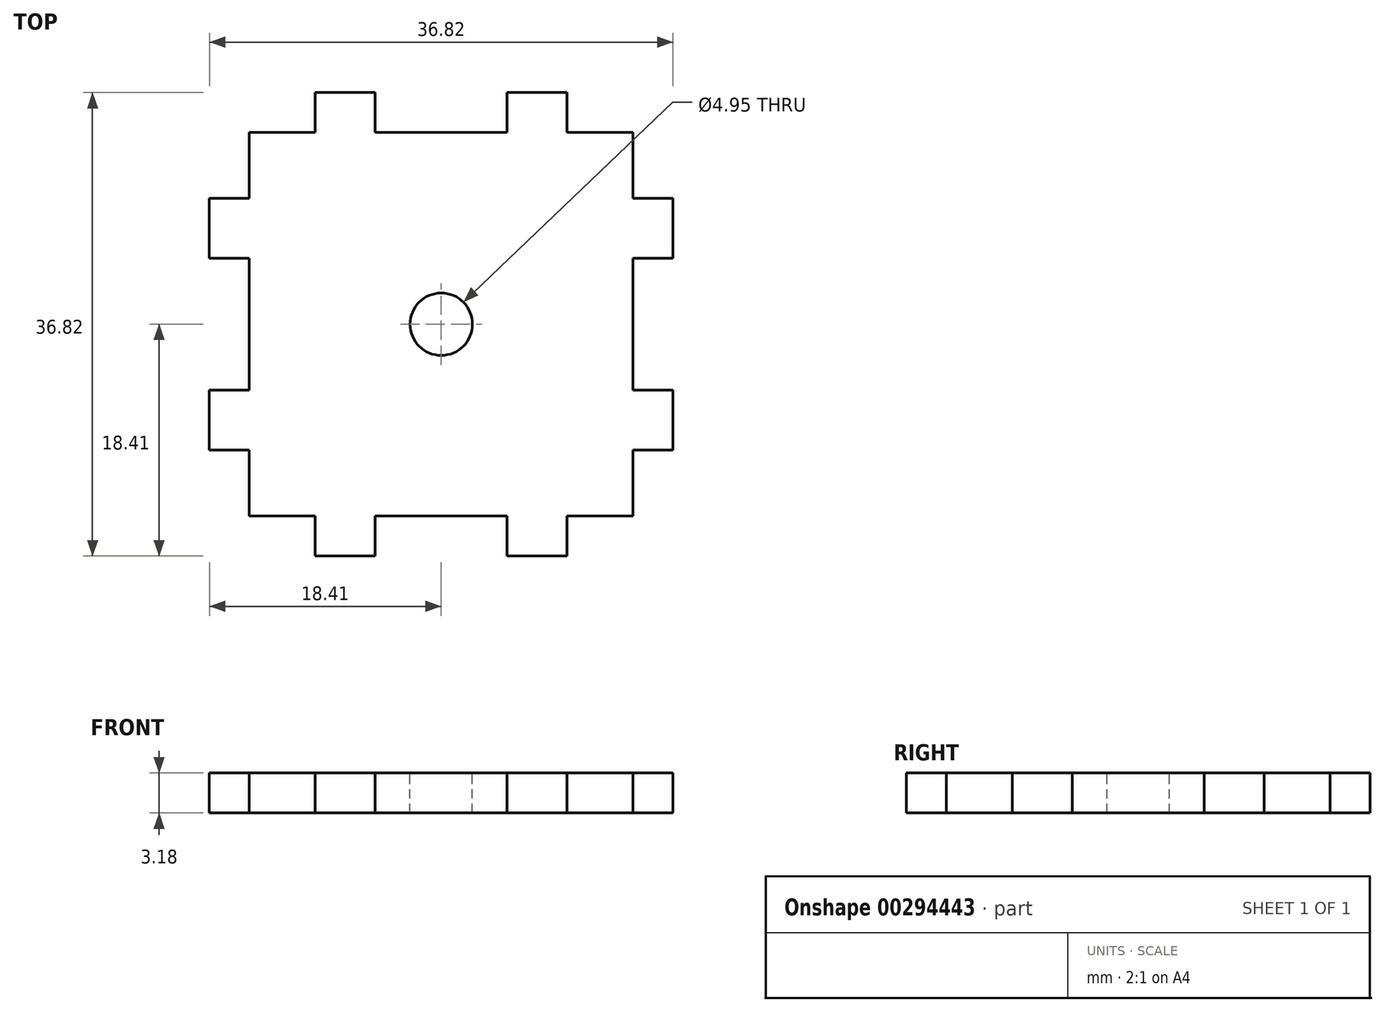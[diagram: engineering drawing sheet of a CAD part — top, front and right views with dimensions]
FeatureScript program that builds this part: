
annotation { "Feature Type Name" : "Feature", "Feature Type Description" : "" }
export const myFeature = defineFeature(function(context is Context, id is Id, definition is map)
    precondition{}
    {
        {
            var Q0;
            Q0=qCreatedBy(makeId("Top.planeOp"),FACE);
            var sketch = newSketch(context, id + "F0", { "sketchPlane" : qUnion([Q0])});
            skLineSegment(sketch, "E0.bottom", {"start": v(15.24, 15.24) * mm, "end": v(-15.24, 15.24) * mm});
            skLineSegment(sketch, "E0.top", {"start": v(15.24, -15.24) * mm, "end": v(-15.24, -15.24) * mm});
            skLineSegment(sketch, "E0.left", {"start": v(15.24, 15.24) * mm, "end": v(15.24, -15.24) * mm});
            skLineSegment(sketch, "E0.right", {"start": v(-15.24, 15.24) * mm, "end": v(-15.24, -15.24) * mm});
            skPoint(sketch, "E0.middle", {"position": v(0, 0) * mm});
            skLineSegment(sketch, "E1", {"start": v(0, 15.24) * mm, "end": v(0, -15.24) * mm});
            skLineSegment(sketch, "E2", {"start": v(-7.62, 15.24) * mm, "end": v(-7.62, -15.24) * mm});
            skLineSegment(sketch, "E3", {"start": v(7.62, 15.24) * mm, "end": v(7.62, -15.24) * mm});
            skLineSegment(sketch, "E4.bottom", {"start": v(-5.24, 18.41) * mm, "end": v(-10, 18.41) * mm});
            skLineSegment(sketch, "E4.top", {"start": v(-5.24, 12.06) * mm, "end": v(-10, 12.06) * mm});
            skLineSegment(sketch, "E4.left", {"start": v(-5.24, 18.41) * mm, "end": v(-5.24, 12.06) * mm});
            skLineSegment(sketch, "E4.right", {"start": v(-10, 18.41) * mm, "end": v(-10, 12.06) * mm});
            skPoint(sketch, "E4.middle", {"position": v(-7.62, 15.24) * mm});
            skLineSegment(sketch, "E5.bottom", {"start": v(10, 18.41) * mm, "end": v(5.24, 18.41) * mm});
            skLineSegment(sketch, "E5.top", {"start": v(10, 12.06) * mm, "end": v(5.24, 12.06) * mm});
            skLineSegment(sketch, "E5.left", {"start": v(10, 18.41) * mm, "end": v(10, 12.06) * mm});
            skLineSegment(sketch, "E5.right", {"start": v(5.24, 18.41) * mm, "end": v(5.24, 12.06) * mm});
            skPoint(sketch, "E5.middle", {"position": v(7.62, 15.24) * mm});
            skLineSegment(sketch, "E6", {"start": v(-15.24, 0) * mm, "end": v(15.24, 0) * mm});
            skLineSegment(sketch, "E7.MirrorCS", {"start": v(5.24, -18.41) * mm, "end": v(5.24, -12.06) * mm});
            skLineSegment(sketch, "E8.MirrorCS", {"start": v(10, -18.41) * mm, "end": v(5.24, -18.41) * mm});
            skLineSegment(sketch, "E9.MirrorCS", {"start": v(10, -18.41) * mm, "end": v(10, -12.06) * mm});
            skLineSegment(sketch, "E10.MirrorCS", {"start": v(7.62, -15.24) * mm, "end": v(7.62, 15.24) * mm});
            skLineSegment(sketch, "E11.MirrorCS", {"start": v(-5.24, -18.41) * mm, "end": v(-5.24, -12.06) * mm});
            skLineSegment(sketch, "E12.MirrorCS", {"start": v(-10, -18.41) * mm, "end": v(-10, -12.06) * mm});
            skLineSegment(sketch, "E13.MirrorCS", {"start": v(-5.24, -18.41) * mm, "end": v(-10, -18.41) * mm});
            skLineSegment(sketch, "E14.MirrorCS", {"start": v(-5.24, -12.06) * mm, "end": v(-10, -12.06) * mm});
            skLineSegment(sketch, "E15.MirrorCS", {"start": v(10, -12.06) * mm, "end": v(5.24, -12.06) * mm});
            skLineSegment(sketch, "E16", {"start": v(-15.24, 7.62) * mm, "end": v(15.24, 7.62) * mm});
            skLineSegment(sketch, "E17", {"start": v(-15.24, -7.62) * mm, "end": v(15.24, -7.62) * mm});
            skLineSegment(sketch, "E18.bottom", {"start": v(-12.06, -5.24) * mm, "end": v(-18.41, -5.24) * mm});
            skLineSegment(sketch, "E18.top", {"start": v(-12.06, -10) * mm, "end": v(-18.41, -10) * mm});
            skLineSegment(sketch, "E18.left", {"start": v(-12.06, -5.24) * mm, "end": v(-12.07, -10) * mm});
            skLineSegment(sketch, "E18.right", {"start": v(-18.41, -5.24) * mm, "end": v(-18.41, -10) * mm});
            skPoint(sketch, "E18.middle", {"position": v(-15.24, -7.62) * mm});
            skLineSegment(sketch, "E19.bottom", {"start": v(-12.07, 10) * mm, "end": v(-18.41, 10) * mm});
            skLineSegment(sketch, "E19.top", {"start": v(-12.06, 5.24) * mm, "end": v(-18.41, 5.24) * mm});
            skLineSegment(sketch, "E19.left", {"start": v(-12.06, 10) * mm, "end": v(-12.06, 5.24) * mm});
            skLineSegment(sketch, "E19.right", {"start": v(-18.41, 10) * mm, "end": v(-18.41, 5.24) * mm});
            skPoint(sketch, "E19.middle", {"position": v(-15.24, 7.62) * mm});
            skLineSegment(sketch, "E20.MirrorCS", {"start": v(12.07, 10) * mm, "end": v(12.07, 5.24) * mm});
            skLineSegment(sketch, "E21.MirrorCS", {"start": v(12.07, 10) * mm, "end": v(18.41, 10) * mm});
            skLineSegment(sketch, "E22.MirrorCS", {"start": v(12.07, 5.24) * mm, "end": v(18.41, 5.24) * mm});
            skLineSegment(sketch, "E23.MirrorCS", {"start": v(18.41, 10) * mm, "end": v(18.41, 5.24) * mm});
            skLineSegment(sketch, "E24.MirrorCS", {"start": v(12.06, -5.24) * mm, "end": v(12.06, -10) * mm});
            skLineSegment(sketch, "E25.MirrorCS", {"start": v(12.06, -5.24) * mm, "end": v(18.41, -5.24) * mm});
            skLineSegment(sketch, "E26.MirrorCS", {"start": v(12.06, -10) * mm, "end": v(18.41, -10) * mm});
            skLineSegment(sketch, "E27.MirrorCS", {"start": v(18.41, -5.24) * mm, "end": v(18.41, -10) * mm});
            skSolve(sketch);
        }
        {
            var Q0;
            {var subQ1=sQuery(id+"F0.wireOp",EDGE,"E4.bottom");Q0=makeQuery(id+"F0.imprint","IMPRINT",FACE,{"disambiguationData":[TD([[makeQuery(id+"F0.imprint","IMPRINT",EDGE,{"derivedFrom":subQ1}),1.0]])]});}
            var Q1;
            {var subQ0=sQuery(id+"F0.wireOp",EDGE,"E2");var subQ1=sQuery(id+"F0.wireOp",EDGE,"E0.bottom");var subQ2=makeQuery(id+"F0.imprint","INTERSECT",VERTEX,{"derivedFrom":[subQ1,subQ0]});Q1=makeQuery(id+"F0.imprint","IMPRINT",FACE,{"disambiguationData":[TD([[makeQuery(id+"F0.imprint","IMPRINT",EDGE,{"disambiguationData":[TD([[subQ2,-1.0]])],"derivedFrom":subQ1}),1.0]])]});}
            var Q2;
            {var subQ0=sQuery(id+"F0.wireOp",EDGE,"E2");var subQ1=sQuery(id+"F0.wireOp",EDGE,"E0.bottom");var subQ2=makeQuery(id+"F0.imprint","INTERSECT",VERTEX,{"derivedFrom":[subQ1,subQ0]});Q2=makeQuery(id+"F0.imprint","IMPRINT",FACE,{"disambiguationData":[TD([[makeQuery(id+"F0.imprint","IMPRINT",EDGE,{"disambiguationData":[TD([[subQ2,1.0]])],"derivedFrom":subQ1}),1.0]])]});}
            var Q3;
            {var subQ5=sQuery(id+"F0.wireOp",EDGE,"E1");var subQ6=sQuery(id+"F0.wireOp",EDGE,"E0.bottom");var subQ7=makeQuery(id+"F0.imprint","INTERSECT",VERTEX,{"derivedFrom":[subQ6,subQ5]});Q3=makeQuery(id+"F0.imprint","IMPRINT",FACE,{"disambiguationData":[TD([[makeQuery(id+"F0.imprint","IMPRINT",EDGE,{"disambiguationData":[TD([[subQ7,-1.0]])],"derivedFrom":subQ6}),1.0]])]});}
            var Q4;
            {var subQ5=sQuery(id+"F0.wireOp",EDGE,"E0.right");var subQ6=sQuery(id+"F0.wireOp",EDGE,"E0.bottom");var subQ7=makeQuery(id+"F0.imprint","INTERSECT",VERTEX,{"derivedFrom":[subQ6,subQ5]});Q4=makeQuery(id+"F0.imprint","IMPRINT",FACE,{"disambiguationData":[TD([[makeQuery(id+"F0.imprint","IMPRINT",EDGE,{"disambiguationData":[TD([[subQ7,1.0]])],"derivedFrom":subQ6}),1.0]])]});}
            var Q5;
            {var subQ0=sQuery(id+"F0.wireOp",EDGE,"E16");var subQ1=sQuery(id+"F0.wireOp",EDGE,"E0.right");var subQ2=makeQuery(id+"F0.imprint","INTERSECT",VERTEX,{"derivedFrom":[subQ1,subQ0]});Q5=makeQuery(id+"F0.imprint","IMPRINT",FACE,{"disambiguationData":[TD([[makeQuery(id+"F0.imprint","IMPRINT",EDGE,{"disambiguationData":[TD([[subQ2,1.0]])],"derivedFrom":subQ1}),1.0]])]});}
            var Q6;
            {var subQ0=sQuery(id+"F0.wireOp",EDGE,"E16");var subQ1=sQuery(id+"F0.wireOp",EDGE,"E0.right");var subQ2=makeQuery(id+"F0.imprint","INTERSECT",VERTEX,{"derivedFrom":[subQ1,subQ0]});Q6=makeQuery(id+"F0.imprint","IMPRINT",FACE,{"disambiguationData":[TD([[makeQuery(id+"F0.imprint","IMPRINT",EDGE,{"disambiguationData":[TD([[subQ2,-1.0]])],"derivedFrom":subQ1}),1.0]])]});}
            var Q7;
            {var subQ0=sQuery(id+"F0.wireOp",EDGE,"E19.right");Q7=makeQuery(id+"F0.imprint","IMPRINT",FACE,{"disambiguationData":[TD([[makeQuery(id+"F0.imprint","IMPRINT",EDGE,{"derivedFrom":subQ0}),1.0]])]});}
            var Q8;
            {var subQ5=sQuery(id+"F0.wireOp",EDGE,"E6");var subQ6=sQuery(id+"F0.wireOp",EDGE,"E0.right");var subQ7=makeQuery(id+"F0.imprint","INTERSECT",VERTEX,{"derivedFrom":[subQ6,subQ5]});Q8=makeQuery(id+"F0.imprint","IMPRINT",FACE,{"disambiguationData":[TD([[makeQuery(id+"F0.imprint","IMPRINT",EDGE,{"disambiguationData":[TD([[subQ7,1.0]])],"derivedFrom":subQ6}),1.0]])]});}
            var Q9;
            {var subQ0=sQuery(id+"F0.wireOp",EDGE,"E16");var subQ1=sQuery(id+"F0.wireOp",EDGE,"E1");var subQ2=makeQuery(id+"F0.imprint","INTERSECT",VERTEX,{"derivedFrom":[subQ1,subQ0]});Q9=makeQuery(id+"F0.imprint","IMPRINT",FACE,{"disambiguationData":[TD([[makeQuery(id+"F0.imprint","IMPRINT",EDGE,{"disambiguationData":[TD([[subQ2,-1.0]])],"derivedFrom":subQ1}),-1.0]])]});}
            var Q10;
            {var subQ0=sQuery(id+"F0.wireOp",EDGE,"E16");var subQ1=sQuery(id+"F0.wireOp",EDGE,"E1");var subQ2=makeQuery(id+"F0.imprint","INTERSECT",VERTEX,{"derivedFrom":[subQ1,subQ0]});Q10=makeQuery(id+"F0.imprint","IMPRINT",FACE,{"disambiguationData":[TD([[makeQuery(id+"F0.imprint","IMPRINT",EDGE,{"disambiguationData":[TD([[subQ2,-1.0]])],"derivedFrom":subQ1}),1.0]])]});}
            var Q11;
            {var subQ3=sQuery(id+"F0.wireOp",EDGE,"E0.bottom");var subQ5=sQuery(id+"F0.wireOp",EDGE,"E1");var subQ6=makeQuery(id+"F0.imprint","INTERSECT",VERTEX,{"derivedFrom":[subQ3,subQ5]});Q11=makeQuery(id+"F0.imprint","IMPRINT",FACE,{"disambiguationData":[TD([[makeQuery(id+"F0.imprint","IMPRINT",EDGE,{"disambiguationData":[TD([[subQ6,1.0]])],"derivedFrom":subQ3}),1.0]])]});}
            var Q12;
            {var subQ0=sQuery(id+"F0.wireOp",EDGE,"E10.MirrorCS");var subQ1=sQuery(id+"F0.wireOp",EDGE,"E0.bottom");var subQ2=makeQuery(id+"F0.imprint","INTERSECT",VERTEX,{"derivedFrom":[subQ1,subQ0]});Q12=makeQuery(id+"F0.imprint","IMPRINT",FACE,{"disambiguationData":[TD([[makeQuery(id+"F0.imprint","IMPRINT",EDGE,{"disambiguationData":[TD([[subQ2,-1.0]])],"derivedFrom":subQ1}),1.0]])]});}
            var Q13;
            {var subQ0=sQuery(id+"F0.wireOp",EDGE,"E10.MirrorCS");var subQ1=sQuery(id+"F0.wireOp",EDGE,"E0.bottom");var subQ2=makeQuery(id+"F0.imprint","INTERSECT",VERTEX,{"derivedFrom":[subQ1,subQ0]});Q13=makeQuery(id+"F0.imprint","IMPRINT",FACE,{"disambiguationData":[TD([[makeQuery(id+"F0.imprint","IMPRINT",EDGE,{"disambiguationData":[TD([[subQ2,1.0]])],"derivedFrom":subQ1}),1.0]])]});}
            var Q14;
            {var subQ1=sQuery(id+"F0.wireOp",EDGE,"E5.bottom");Q14=makeQuery(id+"F0.imprint","IMPRINT",FACE,{"disambiguationData":[TD([[makeQuery(id+"F0.imprint","IMPRINT",EDGE,{"derivedFrom":subQ1}),1.0]])]});}
            var Q15;
            {var subQ5=sQuery(id+"F0.wireOp",EDGE,"E6");var subQ6=sQuery(id+"F0.wireOp",EDGE,"E0.left");var subQ7=makeQuery(id+"F0.imprint","INTERSECT",VERTEX,{"derivedFrom":[subQ6,subQ5]});Q15=makeQuery(id+"F0.imprint","IMPRINT",FACE,{"disambiguationData":[TD([[makeQuery(id+"F0.imprint","IMPRINT",EDGE,{"disambiguationData":[TD([[subQ7,1.0]])],"derivedFrom":subQ6}),-1.0]])]});}
            var Q16;
            {var subQ8=sQuery(id+"F0.wireOp",EDGE,"E0.left");var subQ10=sQuery(id+"F0.wireOp",EDGE,"E0.bottom");var subQ11=makeQuery(id+"F0.imprint","INTERSECT",VERTEX,{"derivedFrom":[subQ10,subQ8]});Q16=makeQuery(id+"F0.imprint","IMPRINT",FACE,{"disambiguationData":[TD([[makeQuery(id+"F0.imprint","IMPRINT",EDGE,{"disambiguationData":[TD([[subQ11,-1.0]])],"derivedFrom":subQ10}),1.0]])]});}
            var Q17;
            {var subQ0=sQuery(id+"F0.wireOp",EDGE,"E16");var subQ1=sQuery(id+"F0.wireOp",EDGE,"E0.left");var subQ2=makeQuery(id+"F0.imprint","INTERSECT",VERTEX,{"derivedFrom":[subQ1,subQ0]});Q17=makeQuery(id+"F0.imprint","IMPRINT",FACE,{"disambiguationData":[TD([[makeQuery(id+"F0.imprint","IMPRINT",EDGE,{"disambiguationData":[TD([[subQ2,1.0]])],"derivedFrom":subQ1}),-1.0]])]});}
            var Q18;
            {var subQ0=sQuery(id+"F0.wireOp",EDGE,"E16");var subQ1=sQuery(id+"F0.wireOp",EDGE,"E0.left");var subQ2=makeQuery(id+"F0.imprint","INTERSECT",VERTEX,{"derivedFrom":[subQ1,subQ0]});Q18=makeQuery(id+"F0.imprint","IMPRINT",FACE,{"disambiguationData":[TD([[makeQuery(id+"F0.imprint","IMPRINT",EDGE,{"disambiguationData":[TD([[subQ2,-1.0]])],"derivedFrom":subQ1}),-1.0]])]});}
            var Q19;
            {var subQ0=sQuery(id+"F0.wireOp",EDGE,"E23.MirrorCS");Q19=makeQuery(id+"F0.imprint","IMPRINT",FACE,{"disambiguationData":[TD([[makeQuery(id+"F0.imprint","IMPRINT",EDGE,{"derivedFrom":subQ0}),-1.0]])]});}
            var Q20;
            {var subQ5=sQuery(id+"F0.wireOp",EDGE,"E6");var subQ6=sQuery(id+"F0.wireOp",EDGE,"E0.left");var subQ7=makeQuery(id+"F0.imprint","INTERSECT",VERTEX,{"derivedFrom":[subQ6,subQ5]});Q20=makeQuery(id+"F0.imprint","IMPRINT",FACE,{"disambiguationData":[TD([[makeQuery(id+"F0.imprint","IMPRINT",EDGE,{"disambiguationData":[TD([[subQ7,-1.0]])],"derivedFrom":subQ6}),-1.0]])]});}
            var Q21;
            {var subQ0=sQuery(id+"F0.wireOp",EDGE,"E17");var subQ1=sQuery(id+"F0.wireOp",EDGE,"E0.left");var subQ2=makeQuery(id+"F0.imprint","INTERSECT",VERTEX,{"derivedFrom":[subQ1,subQ0]});Q21=makeQuery(id+"F0.imprint","IMPRINT",FACE,{"disambiguationData":[TD([[makeQuery(id+"F0.imprint","IMPRINT",EDGE,{"disambiguationData":[TD([[subQ2,1.0]])],"derivedFrom":subQ1}),-1.0]])]});}
            var Q22;
            {var subQ5=sQuery(id+"F0.wireOp",EDGE,"E0.top");var subQ6=sQuery(id+"F0.wireOp",EDGE,"E0.left");var subQ7=makeQuery(id+"F0.imprint","INTERSECT",VERTEX,{"derivedFrom":[subQ6,subQ5]});Q22=makeQuery(id+"F0.imprint","IMPRINT",FACE,{"disambiguationData":[TD([[makeQuery(id+"F0.imprint","IMPRINT",EDGE,{"disambiguationData":[TD([[subQ7,1.0]])],"derivedFrom":subQ6}),-1.0]])]});}
            var Q23;
            {var subQ0=sQuery(id+"F0.wireOp",EDGE,"E27.MirrorCS");Q23=makeQuery(id+"F0.imprint","IMPRINT",FACE,{"disambiguationData":[TD([[makeQuery(id+"F0.imprint","IMPRINT",EDGE,{"derivedFrom":subQ0}),-1.0]])]});}
            var Q24;
            {var subQ0=sQuery(id+"F0.wireOp",EDGE,"E17");var subQ1=sQuery(id+"F0.wireOp",EDGE,"E0.left");var subQ2=makeQuery(id+"F0.imprint","INTERSECT",VERTEX,{"derivedFrom":[subQ1,subQ0]});Q24=makeQuery(id+"F0.imprint","IMPRINT",FACE,{"disambiguationData":[TD([[makeQuery(id+"F0.imprint","IMPRINT",EDGE,{"disambiguationData":[TD([[subQ2,-1.0]])],"derivedFrom":subQ1}),-1.0]])]});}
            var Q25;
            {var subQ0=sQuery(id+"F0.wireOp",EDGE,"E15.MirrorCS");var subQ1=sQuery(id+"F0.wireOp",EDGE,"E7.MirrorCS");var subQ2=makeQuery(id+"F0.imprint","INTERSECT",VERTEX,{"derivedFrom":[subQ1,subQ0]});Q25=makeQuery(id+"F0.imprint","IMPRINT",FACE,{"disambiguationData":[TD([[makeQuery(id+"F0.imprint","IMPRINT",EDGE,{"disambiguationData":[TD([[subQ2,1.0]])],"derivedFrom":subQ1}),-1.0]])]});}
            var Q26;
            {var subQ0=sQuery(id+"F0.wireOp",EDGE,"E10.MirrorCS");var subQ1=sQuery(id+"F0.wireOp",EDGE,"E0.top");var subQ2=makeQuery(id+"F0.imprint","INTERSECT",VERTEX,{"derivedFrom":[subQ1,subQ0]});Q26=makeQuery(id+"F0.imprint","IMPRINT",FACE,{"disambiguationData":[TD([[makeQuery(id+"F0.imprint","IMPRINT",EDGE,{"disambiguationData":[TD([[subQ2,1.0]])],"derivedFrom":subQ1}),-1.0]])]});}
            var Q27;
            {var subQ4=sQuery(id+"F0.wireOp",EDGE,"E8.MirrorCS");Q27=makeQuery(id+"F0.imprint","IMPRINT",FACE,{"disambiguationData":[TD([[makeQuery(id+"F0.imprint","IMPRINT",EDGE,{"derivedFrom":subQ4}),-1.0]])]});}
            var Q28;
            {var subQ5=sQuery(id+"F0.wireOp",EDGE,"E0.top");var subQ6=sQuery(id+"F0.wireOp",EDGE,"E1");var subQ7=makeQuery(id+"F0.imprint","INTERSECT",VERTEX,{"derivedFrom":[subQ6,subQ5]});Q28=makeQuery(id+"F0.imprint","IMPRINT",FACE,{"disambiguationData":[TD([[makeQuery(id+"F0.imprint","IMPRINT",EDGE,{"disambiguationData":[TD([[subQ7,1.0]])],"derivedFrom":subQ6}),1.0]])]});}
            var Q29;
            {var subQ0=sQuery(id+"F0.wireOp",EDGE,"E6");var subQ1=sQuery(id+"F0.wireOp",EDGE,"E1");var subQ2=makeQuery(id+"F0.imprint","INTERSECT",VERTEX,{"derivedFrom":[subQ1,subQ0]});Q29=makeQuery(id+"F0.imprint","IMPRINT",FACE,{"disambiguationData":[TD([[makeQuery(id+"F0.imprint","IMPRINT",EDGE,{"disambiguationData":[TD([[subQ2,-1.0]])],"derivedFrom":subQ1}),1.0]])]});}
            var Q30;
            {var subQ0=sQuery(id+"F0.wireOp",EDGE,"E6");var subQ1=sQuery(id+"F0.wireOp",EDGE,"E1");var subQ2=makeQuery(id+"F0.imprint","INTERSECT",VERTEX,{"derivedFrom":[subQ1,subQ0]});Q30=makeQuery(id+"F0.imprint","IMPRINT",FACE,{"disambiguationData":[TD([[makeQuery(id+"F0.imprint","IMPRINT",EDGE,{"disambiguationData":[TD([[subQ2,-1.0]])],"derivedFrom":subQ1}),-1.0]])]});}
            var Q31;
            {var subQ5=sQuery(id+"F0.wireOp",EDGE,"E6");var subQ6=sQuery(id+"F0.wireOp",EDGE,"E0.right");var subQ7=makeQuery(id+"F0.imprint","INTERSECT",VERTEX,{"derivedFrom":[subQ6,subQ5]});Q31=makeQuery(id+"F0.imprint","IMPRINT",FACE,{"disambiguationData":[TD([[makeQuery(id+"F0.imprint","IMPRINT",EDGE,{"disambiguationData":[TD([[subQ7,-1.0]])],"derivedFrom":subQ6}),1.0]])]});}
            var Q32;
            {var subQ0=sQuery(id+"F0.wireOp",EDGE,"E17");var subQ1=sQuery(id+"F0.wireOp",EDGE,"E0.right");var subQ2=makeQuery(id+"F0.imprint","INTERSECT",VERTEX,{"derivedFrom":[subQ1,subQ0]});Q32=makeQuery(id+"F0.imprint","IMPRINT",FACE,{"disambiguationData":[TD([[makeQuery(id+"F0.imprint","IMPRINT",EDGE,{"disambiguationData":[TD([[subQ2,1.0]])],"derivedFrom":subQ1}),1.0]])]});}
            var Q33;
            {var subQ0=sQuery(id+"F0.wireOp",EDGE,"E17");var subQ1=sQuery(id+"F0.wireOp",EDGE,"E0.right");var subQ2=makeQuery(id+"F0.imprint","INTERSECT",VERTEX,{"derivedFrom":[subQ1,subQ0]});Q33=makeQuery(id+"F0.imprint","IMPRINT",FACE,{"disambiguationData":[TD([[makeQuery(id+"F0.imprint","IMPRINT",EDGE,{"disambiguationData":[TD([[subQ2,-1.0]])],"derivedFrom":subQ1}),1.0]])]});}
            var Q34;
            {var subQ0=sQuery(id+"F0.wireOp",EDGE,"E18.right");Q34=makeQuery(id+"F0.imprint","IMPRINT",FACE,{"disambiguationData":[TD([[makeQuery(id+"F0.imprint","IMPRINT",EDGE,{"derivedFrom":subQ0}),1.0]])]});}
            var Q35;
            {var subQ3=sQuery(id+"F0.wireOp",EDGE,"E0.top");var subQ5=sQuery(id+"F0.wireOp",EDGE,"E0.right");var subQ6=makeQuery(id+"F0.imprint","INTERSECT",VERTEX,{"derivedFrom":[subQ5,subQ3]});Q35=makeQuery(id+"F0.imprint","IMPRINT",FACE,{"disambiguationData":[TD([[makeQuery(id+"F0.imprint","IMPRINT",EDGE,{"disambiguationData":[TD([[subQ6,1.0]])],"derivedFrom":subQ5}),1.0]])]});}
            var Q36;
            {var subQ0=sQuery(id+"F0.wireOp",EDGE,"E0.top");var subQ1=sQuery(id+"F0.wireOp",EDGE,"E1");var subQ2=makeQuery(id+"F0.imprint","INTERSECT",VERTEX,{"derivedFrom":[subQ1,subQ0]});Q36=makeQuery(id+"F0.imprint","IMPRINT",FACE,{"disambiguationData":[TD([[makeQuery(id+"F0.imprint","IMPRINT",EDGE,{"disambiguationData":[TD([[subQ2,1.0]])],"derivedFrom":subQ1}),-1.0]])]});}
            var Q37;
            {var subQ0=sQuery(id+"F0.wireOp",EDGE,"E0.top");var subQ1=sQuery(id+"F0.wireOp",EDGE,"E2");var subQ2=makeQuery(id+"F0.imprint","INTERSECT",VERTEX,{"derivedFrom":[subQ1,subQ0]});Q37=makeQuery(id+"F0.imprint","IMPRINT",FACE,{"disambiguationData":[TD([[makeQuery(id+"F0.imprint","IMPRINT",EDGE,{"disambiguationData":[TD([[subQ2,1.0]])],"derivedFrom":subQ1}),1.0]])]});}
            var Q38;
            {var subQ0=sQuery(id+"F0.wireOp",EDGE,"E0.top");var subQ1=sQuery(id+"F0.wireOp",EDGE,"E2");var subQ2=makeQuery(id+"F0.imprint","INTERSECT",VERTEX,{"derivedFrom":[subQ1,subQ0]});Q38=makeQuery(id+"F0.imprint","IMPRINT",FACE,{"disambiguationData":[TD([[makeQuery(id+"F0.imprint","IMPRINT",EDGE,{"disambiguationData":[TD([[subQ2,1.0]])],"derivedFrom":subQ1}),-1.0]])]});}
            var Q39;
            {var subQ0=sQuery(id+"F0.wireOp",EDGE,"E13.MirrorCS");Q39=makeQuery(id+"F0.imprint","IMPRINT",FACE,{"disambiguationData":[TD([[makeQuery(id+"F0.imprint","IMPRINT",EDGE,{"derivedFrom":subQ0}),-1.0]])]});}
            extrude(context, id + "F1", {"entities" : qUnion([Q0, Q1, Q2, Q3, Q4, Q5, Q6, Q7, Q8, Q9, Q10, Q11, Q12, Q13, Q14, Q15, Q16, Q17, Q18, Q19, Q20, Q21, Q22, Q23, Q24, Q25, Q26, Q27, Q28, Q29, Q30, Q31, Q32, Q33, Q34, Q35, Q36, Q37, Q38, Q39]), "depth" : 3.17 * mm});
        }
        {
            var Q0;
            Q0=makeQuery(id+"F1.opExtrude","CAP_FACE",FACE,{"disambiguationData":[OSD([sQuery(id+"F0.wireOp",EDGE,"E0.bottom"),sQuery(id+"F0.wireOp",EDGE,"E0.left"),sQuery(id+"F0.wireOp",EDGE,"E0.right"),sQuery(id+"F0.wireOp",EDGE,"E4.bottom"),sQuery(id+"F0.wireOp",EDGE,"E4.left"),sQuery(id+"F0.wireOp",EDGE,"E4.right"),sQuery(id+"F0.wireOp",EDGE,"E5.bottom"),sQuery(id+"F0.wireOp",EDGE,"E5.left"),sQuery(id+"F0.wireOp",EDGE,"E5.right"),sQuery(id+"F0.wireOp",EDGE,"E7.MirrorCS"),sQuery(id+"F0.wireOp",EDGE,"E8.MirrorCS"),sQuery(id+"F0.wireOp",EDGE,"E0.top"),sQuery(id+"F0.wireOp",EDGE,"E9.MirrorCS"),sQuery(id+"F0.wireOp",EDGE,"E11.MirrorCS"),sQuery(id+"F0.wireOp",EDGE,"E12.MirrorCS"),sQuery(id+"F0.wireOp",EDGE,"E13.MirrorCS"),sQuery(id+"F0.wireOp",EDGE,"E18.bottom"),sQuery(id+"F0.wireOp",EDGE,"E18.top"),sQuery(id+"F0.wireOp",EDGE,"E18.right"),sQuery(id+"F0.wireOp",EDGE,"E19.bottom"),sQuery(id+"F0.wireOp",EDGE,"E19.top"),sQuery(id+"F0.wireOp",EDGE,"E19.right"),sQuery(id+"F0.wireOp",EDGE,"E21.MirrorCS"),sQuery(id+"F0.wireOp",EDGE,"E22.MirrorCS"),sQuery(id+"F0.wireOp",EDGE,"E23.MirrorCS"),sQuery(id+"F0.wireOp",EDGE,"E25.MirrorCS"),sQuery(id+"F0.wireOp",EDGE,"E26.MirrorCS"),sQuery(id+"F0.wireOp",EDGE,"E27.MirrorCS")])],"isStart":false});
            var sketch = newSketch(context, id + "F2", { "sketchPlane" : qUnion([Q0])});
            skCircle(sketch, "E28", {"center": v(0, 0) * mm, "radius": 2.48 * mm});
            skSolve(sketch);
        }
        {
            var Q0;
            Q0=makeQuery(id+"F2.imprint","IMPRINT",FACE,{"disambiguationData":[TD([[makeQuery(id+"F2.imprint","IMPRINT",EDGE,{"derivedFrom":sQuery(id+"F2.wireOp",EDGE,"E28")}),1.0]])]});
            extrude(context, id + "F3", {"entities" : qUnion([Q0]), "operationType" : NewBodyOperationType.REMOVE, "oppositeDirection" : true, "depth" : 25.4 * mm});
        }
    });
